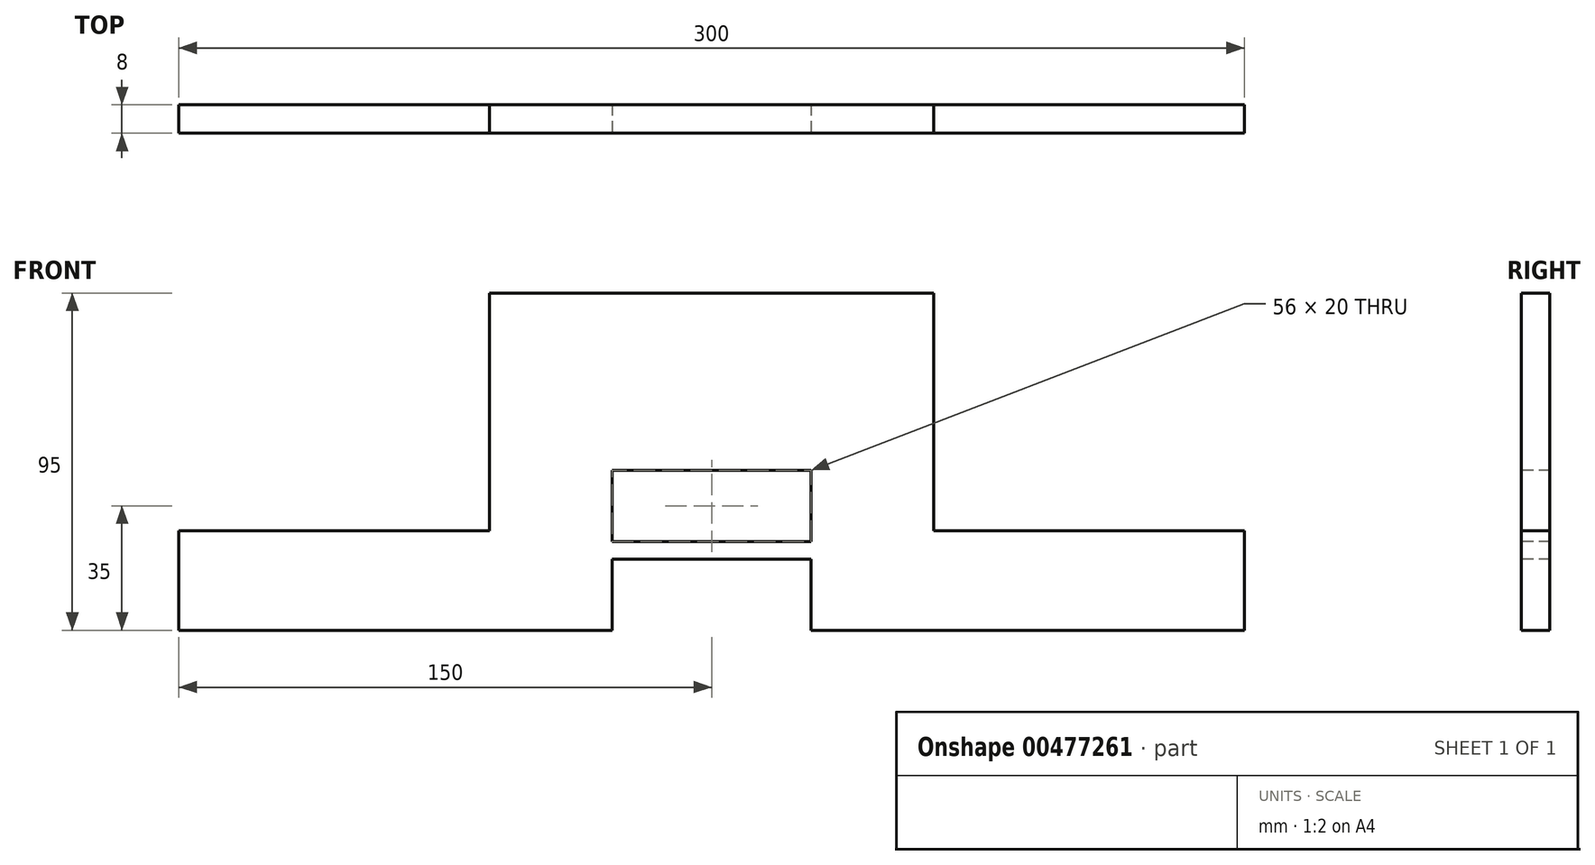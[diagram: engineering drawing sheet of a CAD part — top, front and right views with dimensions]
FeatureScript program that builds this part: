
annotation { "Feature Type Name" : "Feature", "Feature Type Description" : "" }
export const myFeature = defineFeature(function(context is Context, id is Id, definition is map)
    precondition{}
    {
        {
            var Q0;
            Q0=qCreatedBy(makeId("Front.planeOp"),FACE);
            var sketch = newSketch(context, id + "F0", { "sketchPlane" : qUnion([Q0])});
            skLineSegment(sketch, "E0", {"start": v(0, 0) * mm, "end": v(150, 0) * mm});
            skLineSegment(sketch, "E1", {"start": v(150, 0) * mm, "end": v(150, 28) * mm});
            skLineSegment(sketch, "E2", {"start": v(150, 28) * mm, "end": v(62.5, 28) * mm});
            skLineSegment(sketch, "E3", {"start": v(62.5, 28) * mm, "end": v(62.5, 95) * mm});
            skLineSegment(sketch, "E4", {"start": v(62.5, 95) * mm, "end": v(-62.5, 95) * mm});
            skLineSegment(sketch, "E5", {"start": v(-62.5, 95) * mm, "end": v(-62.5, 28) * mm});
            skLineSegment(sketch, "E6", {"start": v(-62.5, 28) * mm, "end": v(-150, 28) * mm});
            skLineSegment(sketch, "E7", {"start": v(-150, 28) * mm, "end": v(-150, 0) * mm});
            skLineSegment(sketch, "E8", {"start": v(-150, 0) * mm, "end": v(0, 0) * mm});
            skSolve(sketch);
        }
        {
            var Q0;
            Q0=makeQuery(id+"F0.imprint","IMPRINT",FACE,{"disambiguationData":[TD([[makeQuery(id+"F0.imprint","IMPRINT",EDGE,{"derivedFrom":sQuery(id+"F0.wireOp",EDGE,"E0")}),1.0]])]});
            extrude(context, id + "F1", {"entities" : qUnion([Q0]), "depth" : 8 * mm});
        }
        {
            var Q0;
            Q0=makeQuery(id+"F1.opExtrude","CAP_FACE",FACE,{"disambiguationData":[OSD([sQuery(id+"F0.wireOp",EDGE,"E0"),sQuery(id+"F0.wireOp",EDGE,"E1"),sQuery(id+"F0.wireOp",EDGE,"E2"),sQuery(id+"F0.wireOp",EDGE,"E3"),sQuery(id+"F0.wireOp",EDGE,"E4"),sQuery(id+"F0.wireOp",EDGE,"E5"),sQuery(id+"F0.wireOp",EDGE,"E6"),sQuery(id+"F0.wireOp",EDGE,"E7"),sQuery(id+"F0.wireOp",EDGE,"E8")])],"isStart":false});
            var sketch = newSketch(context, id + "F2", { "sketchPlane" : qUnion([Q0])});
            skLineSegment(sketch, "E9.bottom", {"start": v(-28, 0) * mm, "end": v(28, 0) * mm});
            skLineSegment(sketch, "E9.top", {"start": v(-28, 20) * mm, "end": v(28, 20) * mm});
            skLineSegment(sketch, "E9.left", {"start": v(-28, 0) * mm, "end": v(-28, 20) * mm});
            skLineSegment(sketch, "E9.right", {"start": v(28, 0) * mm, "end": v(28, 20) * mm});
            skSolve(sketch);
        }
        {
            var Q0;
            Q0=makeQuery(id+"F2.imprint","IMPRINT",FACE,{"disambiguationData":[TD([[makeQuery(id+"F2.imprint","IMPRINT",EDGE,{"derivedFrom":sQuery(id+"F2.wireOp",EDGE,"E9.bottom")}),1.0]])]});
            extrude(context, id + "F3", {"entities" : qUnion([Q0]), "operationType" : NewBodyOperationType.REMOVE, "oppositeDirection" : true, "depth" : 25 * mm});
        }
        {
            var Q0;
            Q0=makeQuery(id+"F1.opExtrude","CAP_FACE",FACE,{"disambiguationData":[OSD([sQuery(id+"F0.wireOp",EDGE,"E0"),sQuery(id+"F0.wireOp",EDGE,"E1"),sQuery(id+"F0.wireOp",EDGE,"E2"),sQuery(id+"F0.wireOp",EDGE,"E3"),sQuery(id+"F0.wireOp",EDGE,"E4"),sQuery(id+"F0.wireOp",EDGE,"E5"),sQuery(id+"F0.wireOp",EDGE,"E6"),sQuery(id+"F0.wireOp",EDGE,"E7"),sQuery(id+"F0.wireOp",EDGE,"E8")])],"isStart":false});
            var sketch = newSketch(context, id + "F4", { "sketchPlane" : qUnion([Q0])});
            skSolve(sketch);
        }
        {
            var Q0;
            {var subQ5=sQuery(id+"F0.wireOp",EDGE,"E1");Q0=makeQuery(id+"F4.imprint","IMPRINT",FACE,{"disambiguationData":[TD([[makeQuery(id+"F4.imprint","IMPRINT",EDGE,{"derivedFrom":makeQuery(id+"F1.opExtrude","CAP_EDGE",EDGE,{"disambiguationData":[OSD([subQ5])],"isStart":false})}),1.0]])]});}
            var sketch = newSketch(context, id + "F5", { "sketchPlane" : qUnion([Q0])});
            skLineSegment(sketch, "E10", {"start": v(0, 0) * mm, "end": v(0, 95) * mm});
            skLineSegment(sketch, "E11", {"start": v(0, 95) * mm, "end": v(0, 45) * mm});
            skLineSegment(sketch, "E12.bottom", {"start": v(0, 45) * mm, "end": v(-28, 45) * mm});
            skLineSegment(sketch, "E12.top", {"start": v(0, 25) * mm, "end": v(-28, 25) * mm});
            skLineSegment(sketch, "E12.left", {"start": v(0, 45) * mm, "end": v(0, 25) * mm});
            skLineSegment(sketch, "E12.right", {"start": v(-28, 45) * mm, "end": v(-28, 25) * mm});
            skLineSegment(sketch, "E13.bottom", {"start": v(0, 25) * mm, "end": v(28, 25) * mm});
            skLineSegment(sketch, "E13.top", {"start": v(0, 45) * mm, "end": v(28, 45) * mm});
            skLineSegment(sketch, "E13.left", {"start": v(0, 25) * mm, "end": v(0, 45) * mm});
            skLineSegment(sketch, "E13.right", {"start": v(28, 25) * mm, "end": v(28, 45) * mm});
            skSolve(sketch);
        }
        {
            var Q0;
            Q0=makeQuery(id+"F5.imprint","IMPRINT",FACE,{"disambiguationData":[TD([[makeQuery(id+"F5.imprint","IMPRINT",EDGE,{"derivedFrom":sQuery(id+"F5.wireOp",EDGE,"E12.bottom")}),1.0]])]});
            var Q1;
            Q1=makeQuery(id+"F5.imprint","IMPRINT",FACE,{"disambiguationData":[TD([[makeQuery(id+"F5.imprint","IMPRINT",EDGE,{"derivedFrom":sQuery(id+"F5.wireOp",EDGE,"E13.bottom")}),1.0]])]});
            extrude(context, id + "F6", {"entities" : qUnion([Q0, Q1]), "operationType" : NewBodyOperationType.REMOVE, "oppositeDirection" : true, "depth" : 25 * mm});
        }
    });
